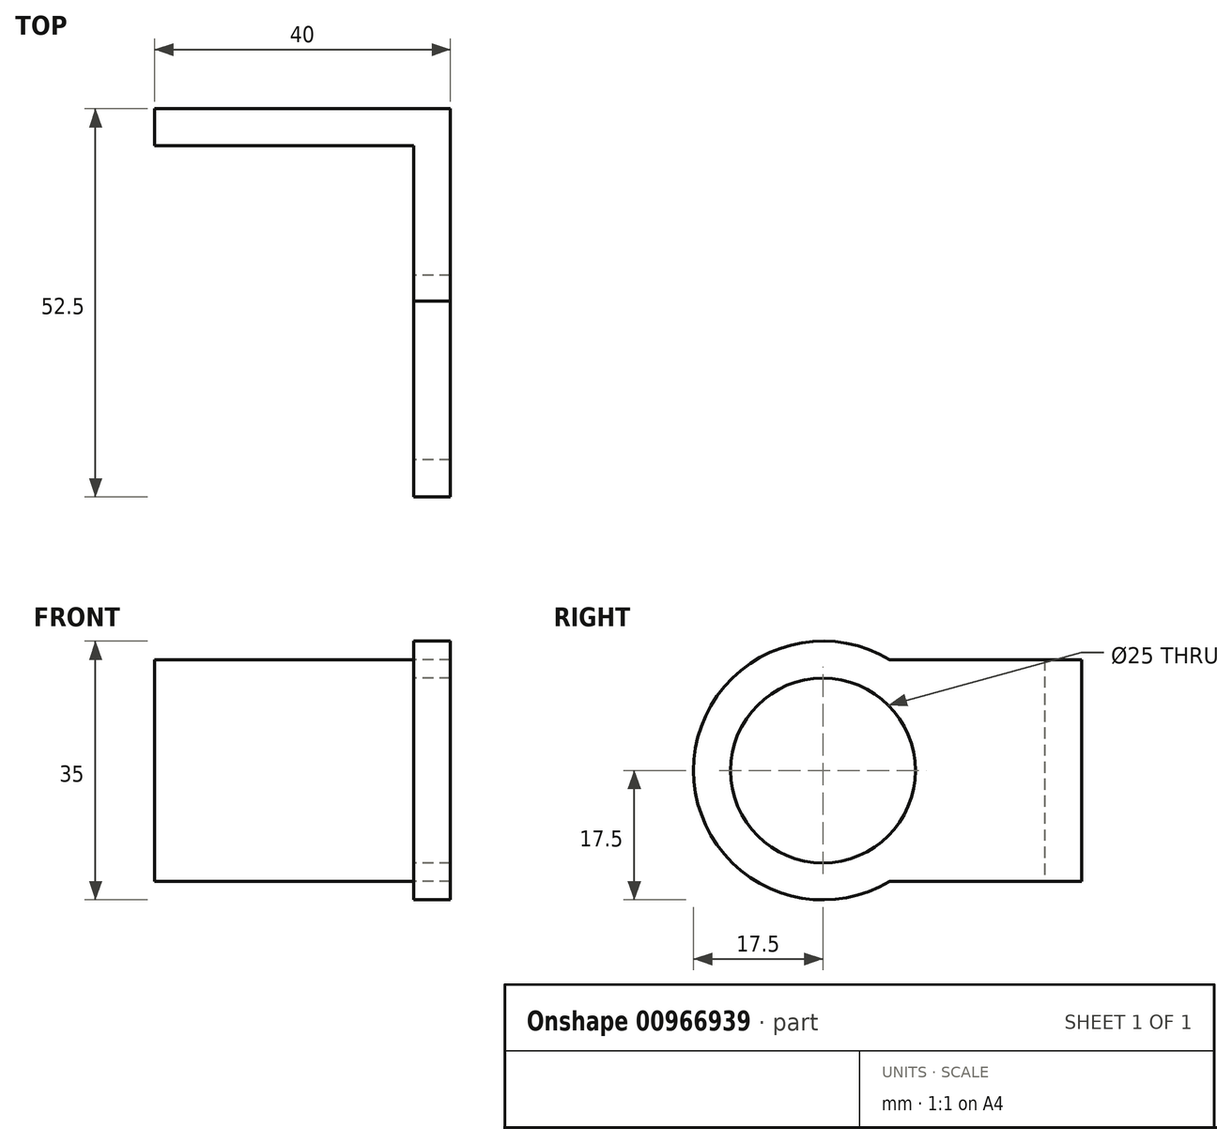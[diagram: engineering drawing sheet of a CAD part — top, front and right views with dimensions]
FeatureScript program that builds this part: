
annotation { "Feature Type Name" : "Feature", "Feature Type Description" : "" }
export const myFeature = defineFeature(function(context is Context, id is Id, definition is map)
    precondition{}
    {
        {
            var Q0;
            Q0=qCreatedBy(makeId("Right.planeOp"),FACE);
            var sketch = newSketch(context, id + "F0", { "sketchPlane" : qUnion([Q0])});
            skLineSegment(sketch, "E0.bottom", {"start": v(0, 0) * mm, "end": v(10, 0) * mm});
            skLineSegment(sketch, "E0.top", {"start": v(0, -30) * mm, "end": v(10, -30) * mm});
            skLineSegment(sketch, "E0.right", {"start": v(10, 0) * mm, "end": v(10, -30) * mm});
            skArc(sketch, "E1", {"start": v(-10.99, 0) * mm, "mid": v(-37.5, -15) * mm, "end": v(-10.99, -30) * mm});
            skLineSegment(sketch, "E2", {"start": v(0, 0) * mm, "end": v(-10.99, 0) * mm});
            skLineSegment(sketch, "E3", {"start": v(0, -30) * mm, "end": v(-10.99, -30) * mm});
            skCircle(sketch, "E4", {"center": v(-20, -15) * mm, "radius": 12.5 * mm});
            skPoint(sketch, "E5.start.orphan", {"position": v(0, -15) * mm});
            skSolve(sketch);
        }
        {
            var Q0;
            Q0 = qSketchRegion(id + "F0", true);
            extrude(context, id + "F1", {"entities" : qUnion([Q0]), "depth" : 5 * mm, "offsetDistance" : 25 * mm});
        }
        {
            var Q0;
            Q0=qCreatedBy(makeId("Top.planeOp"),FACE);
            var sketch = newSketch(context, id + "F2", { "sketchPlane" : qUnion([Q0])});
            skLineSegment(sketch, "E6", {"start": v(0, 0) * mm, "end": v(0, 10) * mm});
            skLineSegment(sketch, "E7", {"start": v(0, 10) * mm, "end": v(5, 10) * mm});
            skLineSegment(sketch, "E8", {"start": v(5, 10) * mm, "end": v(5, 15) * mm});
            skLineSegment(sketch, "E9", {"start": v(5, 15) * mm, "end": v(-35, 15) * mm});
            skLineSegment(sketch, "E10", {"start": v(0, 10) * mm, "end": v(-15, 10) * mm});
            skLineSegment(sketch, "E11", {"start": v(-15, 10) * mm, "end": v(-35, 10) * mm});
            skLineSegment(sketch, "E12", {"start": v(-35, 15) * mm, "end": v(-35, 10) * mm});
            skSolve(sketch);
        }
        {
            var Q0;
            Q0 = qSketchRegion(id + "F2", true);
            extrude(context, id + "F3", {"entities" : qUnion([Q0]), "operationType" : NewBodyOperationType.ADD, "oppositeDirection" : true, "depth" : 30 * mm, "offsetDistance" : 25 * mm});
        }
    });
